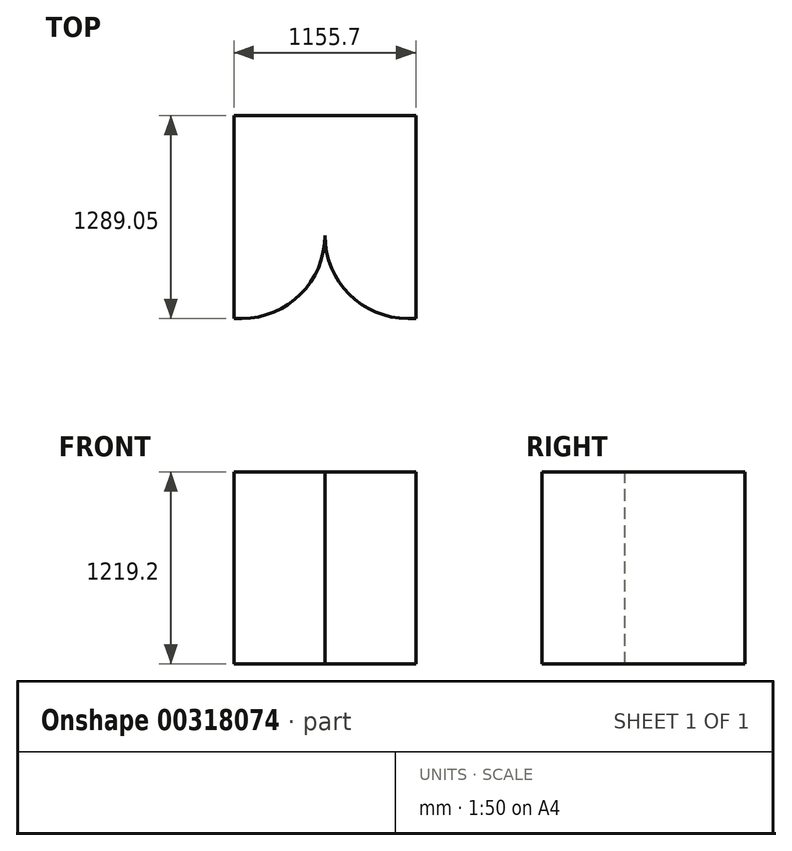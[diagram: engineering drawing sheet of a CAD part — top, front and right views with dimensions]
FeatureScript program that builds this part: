
annotation { "Feature Type Name" : "Feature", "Feature Type Description" : "" }
export const myFeature = defineFeature(function(context is Context, id is Id, definition is map)
    precondition{}
    {
        {
            var Q0;
            Q0=qCreatedBy(makeId("Front.planeOp"),FACE);
            var sketch = newSketch(context, id + "F0", { "sketchPlane" : qUnion([Q0])});
            skLineSegment(sketch, "E0.bottom", {"start": v(-1155.7, 1219.2) * mm, "end": v(0, 1219.2) * mm});
            skLineSegment(sketch, "E0.top", {"start": v(-1155.7, 0) * mm, "end": v(0, 0) * mm});
            skLineSegment(sketch, "E0.left", {"start": v(-1155.7, 1219.2) * mm, "end": v(-1155.7, 0) * mm});
            skLineSegment(sketch, "E0.right", {"start": v(0, 1219.2) * mm, "end": v(0, 0) * mm});
            skSolve(sketch);
        }
        {
            var Q0;
            Q0=qSketchRegion(id+"F0",true);
            extrude(context, id + "F1", {"entities" : qUnion([Q0]), "depth" : 1289.05 * mm, "offsetDistance" : 25.4 * mm});
        }
        {
            var Q0;
            Q0=makeQuery(id+"F1.opExtrude","SWEPT_FACE",FACE,{"disambiguationData":[OSD([sQuery(id+"F0.wireOp",EDGE,"E0.bottom")])]});
            var sketch = newSketch(context, id + "F2", { "sketchPlane" : qUnion([Q0])});
            skArc(sketch, "E1", {"start": v(-1104.9, -1289.05) * mm, "mid": v(-732.22, -1134.68) * mm, "end": v(-577.85, -762) * mm});
            skArc(sketch, "E2", {"start": v(-577.85, -762) * mm, "mid": v(-423.48, -1134.68) * mm, "end": v(-50.8, -1289.05) * mm});
            skLineSegment(sketch, "E3", {"start": v(-1155.7, -762) * mm, "end": v(0, -762) * mm, "construction": true});
            skLineSegment(sketch, "E4.0", {"start": v(0, -1289.05) * mm, "end": v(0, 0) * mm});
            skLineSegment(sketch, "E5.0", {"start": v(-1155.7, -1289.05) * mm, "end": v(-1155.7, 0) * mm});
            skSolve(sketch);
        }
        {
            var Q0;
            {var subQ0=sQuery(id+"F2.wireOp",EDGE,"E1");Q0=makeQuery(id+"F2.imprint","IMPRINT",FACE,{"disambiguationData":[TD([[makeQuery(id+"F2.imprint","IMPRINT",EDGE,{"derivedFrom":subQ0}),-1.0]])]});}
            extrude(context, id + "F3", {"entities" : qUnion([Q0]), "operationType" : NewBodyOperationType.REMOVE, "endBound" : BoundingType.UP_TO_NEXT, "oppositeDirection" : true, "depth" : 50.8 * mm, "offsetDistance" : 25.4 * mm});
        }
    });
